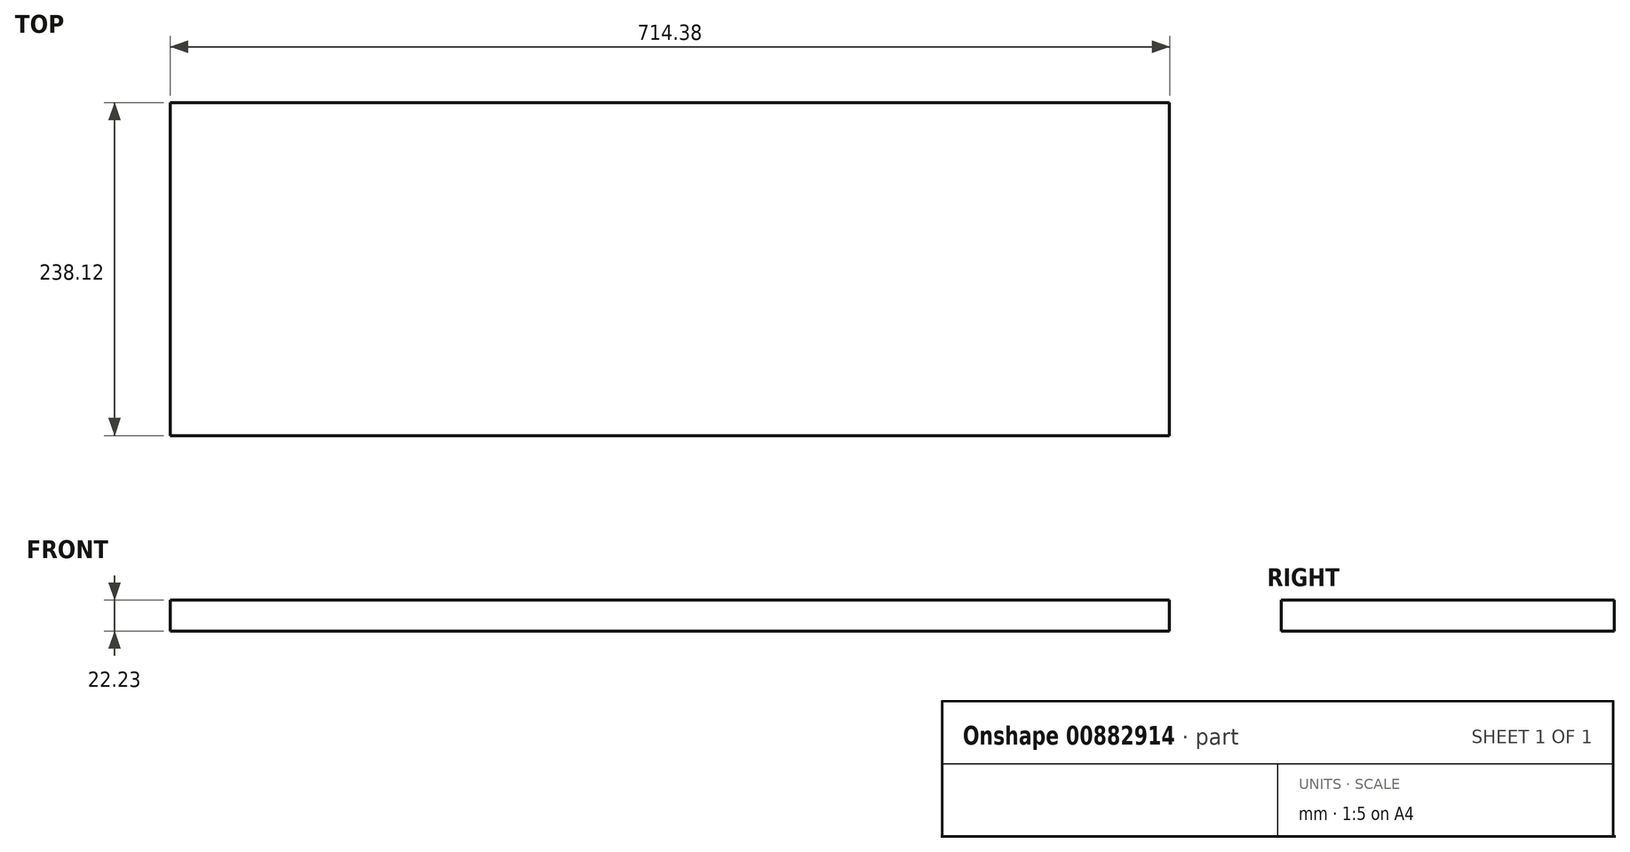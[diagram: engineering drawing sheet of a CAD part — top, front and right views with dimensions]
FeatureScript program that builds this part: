
annotation { "Feature Type Name" : "Feature", "Feature Type Description" : "" }
export const myFeature = defineFeature(function(context is Context, id is Id, definition is map)
    precondition{}
    {
        {
            var Q0;
            Q0=qCreatedBy(makeId("Front.planeOp"),FACE);
            var sketch = newSketch(context, id + "F0", { "sketchPlane" : qUnion([Q0])});
            skLineSegment(sketch, "E0.bottom", {"start": v(0, 0) * mm, "end": v(714.38, 0) * mm});
            skLineSegment(sketch, "E0.top", {"start": v(0, -22.22) * mm, "end": v(714.38, -22.22) * mm});
            skLineSegment(sketch, "E0.left", {"start": v(0, 0) * mm, "end": v(0, -22.22) * mm});
            skLineSegment(sketch, "E0.right", {"start": v(714.38, 0) * mm, "end": v(714.38, -22.22) * mm});
            skSolve(sketch);
        }
        {
            var Q0;
            Q0=makeQuery(id+"F0.imprint","IMPRINT",FACE,{"disambiguationData":[TD([[makeQuery(id+"F0.imprint","IMPRINT",EDGE,{"derivedFrom":sQuery(id+"F0.wireOp",EDGE,"E0.bottom")}),-1.0]])]});
            extrude(context, id + "F1", {"entities" : qUnion([Q0]), "depth" : 238.12 * mm, "offsetDistance" : 25.4 * mm});
        }
    });
